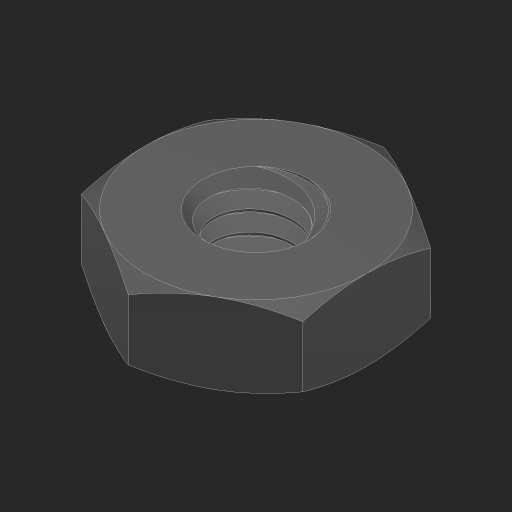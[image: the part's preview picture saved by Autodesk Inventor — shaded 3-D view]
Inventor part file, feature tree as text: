
AUTODESK INVENTOR PART (.ipt)
format: ipt  version: 2023 (Build 270158000, 158)  size: 271,360 bytes
history: native  units: in
note: dims shown in document units (in); Inventor stores cm internally (conversion verified against a paired STEP export)
features: other x4, sketch x1, mirror x1, extrude x1
ambient origin geometry x8: Origin, YZ Plane, XZ Plane, XY Plane, X Axis, Y Axis, Z Axis, Center Point
bodies: Solid1 (feature_tree)
feature tree (7):
  other  "Nut Nylon - White"
  other  "Table"
  other  "Nut Nylon - Black"
  sketch  "Sketch1"  dims[d0=0.001in d1=0.125in d2=0.0in]
  other  "Srf1"
  mirror  "Mirror1"
  extrude  "ExtrusionSrf1"  Depth=0.125in TaperAngle=0.0deg
